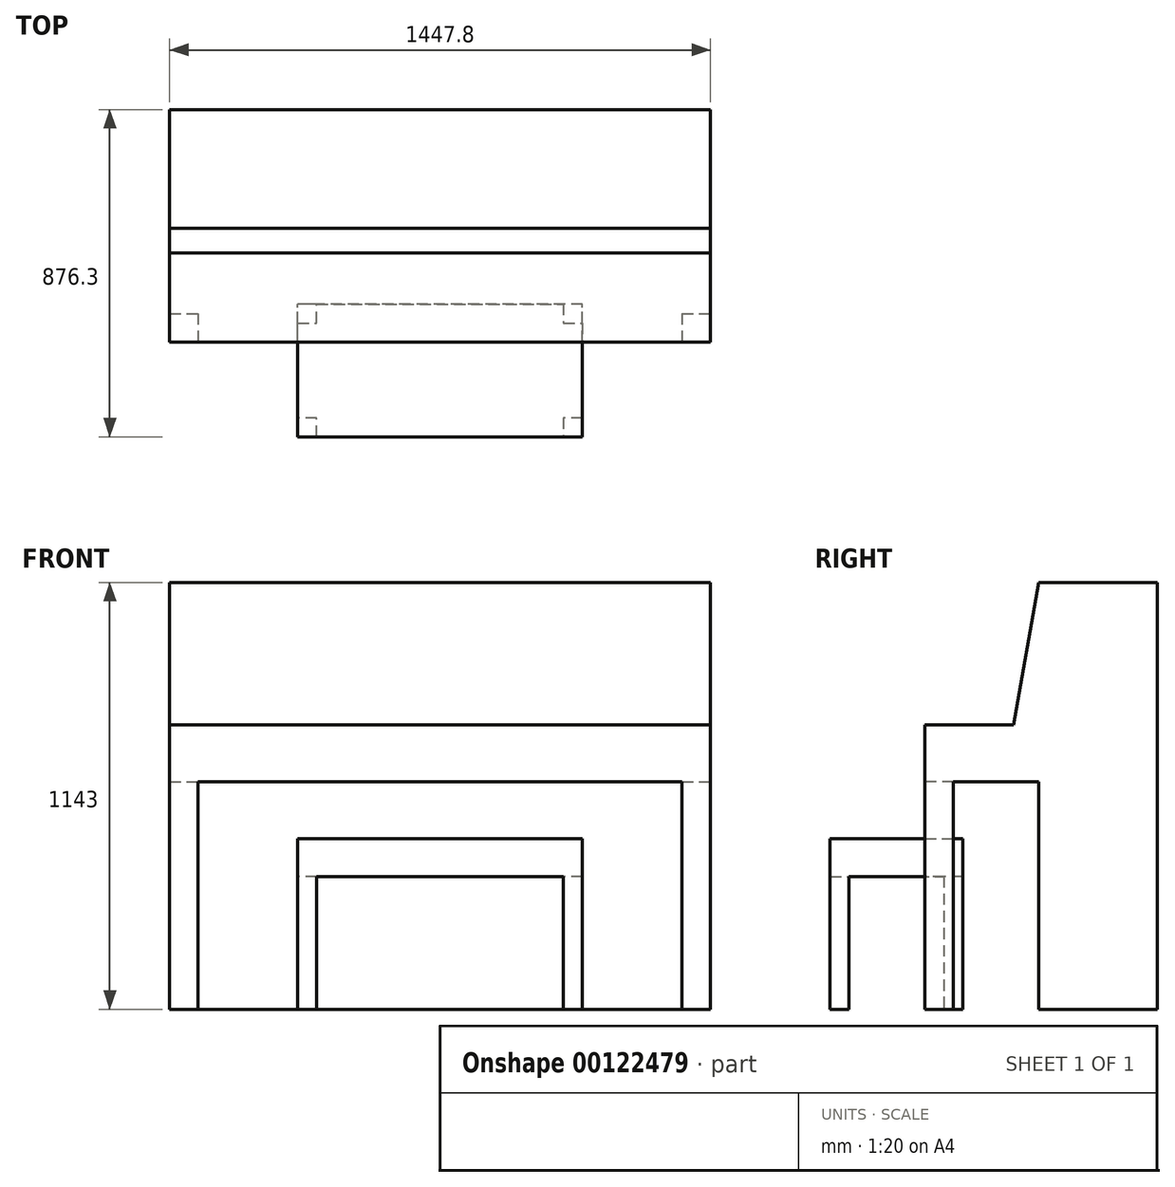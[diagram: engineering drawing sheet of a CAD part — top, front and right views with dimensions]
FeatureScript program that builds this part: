
annotation { "Feature Type Name" : "Feature", "Feature Type Description" : "" }
export const myFeature = defineFeature(function(context is Context, id is Id, definition is map)
    precondition{}
    {
        {
            var Q0;
            Q0=qCreatedBy(makeId("Top.planeOp"),FACE);
            var sketch = newSketch(context, id + "F0", { "sketchPlane" : qUnion([Q0])});
            skLineSegment(sketch, "E0.bottom", {"start": v(0, 0) * mm, "end": v(1447.8, 0) * mm});
            skLineSegment(sketch, "E0.top", {"start": v(0, -622.3) * mm, "end": v(1447.8, -622.3) * mm});
            skLineSegment(sketch, "E0.left", {"start": v(0, 0) * mm, "end": v(0, -622.3) * mm});
            skLineSegment(sketch, "E0.right", {"start": v(1447.8, 0) * mm, "end": v(1447.8, -622.3) * mm});
            skSolve(sketch);
        }
        {
            var Q0;
            Q0 = qSketchRegion(id + "F0", true);
            extrude(context, id + "F1", {"entities" : qUnion([Q0]), "depth" : 1143 * mm});
        }
        {
            var Q0;
            Q0=makeQuery(id+"F1.opExtrude","SWEPT_FACE",FACE,{"disambiguationData":[OSD([sQuery(id+"F0.wireOp",EDGE,"E0.right")])]});
            var sketch = newSketch(context, id + "F2", { "sketchPlane" : qUnion([Q0])});
            skLineSegment(sketch, "E1", {"start": v(-622.3, 1143) * mm, "end": v(-622.3, 762) * mm});
            skLineSegment(sketch, "E2", {"start": v(-622.3, 762) * mm, "end": v(-384.68, 762) * mm});
            skLineSegment(sketch, "E3", {"start": v(-384.68, 762) * mm, "end": v(-317.5, 1143) * mm});
            skLineSegment(sketch, "E4", {"start": v(-317.5, 1143) * mm, "end": v(-622.3, 1143) * mm});
            skSolve(sketch);
        }
        {
            var Q0;
            Q0 = qSketchRegion(id + "F2", true);
            extrude(context, id + "F3", {"entities" : qUnion([Q0]), "operationType" : NewBodyOperationType.REMOVE, "endBound" : BoundingType.THROUGH_ALL, "oppositeDirection" : true, "depth" : 25.4 * mm});
        }
        {
            var Q0;
            Q0=makeQuery(id+"F1.opExtrude","SWEPT_FACE",FACE,{"disambiguationData":[OSD([sQuery(id+"F0.wireOp",EDGE,"E0.top")])]});
            var sketch = newSketch(context, id + "F4", { "sketchPlane" : qUnion([Q0])});
            skLineSegment(sketch, "E5.bottom", {"start": v(76.2, 0) * mm, "end": v(1371.6, 0) * mm});
            skLineSegment(sketch, "E5.top", {"start": v(76.2, 609.6) * mm, "end": v(1371.6, 609.6) * mm});
            skLineSegment(sketch, "E5.left", {"start": v(76.2, 0) * mm, "end": v(76.2, 609.6) * mm});
            skLineSegment(sketch, "E5.right", {"start": v(1371.6, 0) * mm, "end": v(1371.6, 609.6) * mm});
            skPoint(sketch, "E5.middle", {"position": v(723.9, 304.8) * mm});
            skSolve(sketch);
        }
        {
            var Q0;
            Q0 = qSketchRegion(id + "F4", true);
            extrude(context, id + "F5", {"entities" : qUnion([Q0]), "operationType" : NewBodyOperationType.REMOVE, "oppositeDirection" : true, "depth" : 304.8 * mm});
        }
        {
            var Q0;
            Q0=makeQuery(id+"F1.opExtrude","SWEPT_FACE",FACE,{"disambiguationData":[OSD([sQuery(id+"F0.wireOp",EDGE,"E0.right")])]});
            var sketch = newSketch(context, id + "F6", { "sketchPlane" : qUnion([Q0])});
            skLineSegment(sketch, "E6.bottom", {"start": v(-546.1, 0) * mm, "end": v(-317.5, 0) * mm});
            skLineSegment(sketch, "E6.top", {"start": v(-546.1, 609.6) * mm, "end": v(-317.5, 609.6) * mm});
            skLineSegment(sketch, "E6.left", {"start": v(-546.1, 0) * mm, "end": v(-546.1, 609.6) * mm});
            skLineSegment(sketch, "E6.right", {"start": v(-317.5, 0) * mm, "end": v(-317.5, 609.6) * mm});
            skPoint(sketch, "E6.middle", {"position": v(-431.8, 304.8) * mm});
            skSolve(sketch);
        }
        {
            var Q0;
            Q0 = qSketchRegion(id + "F6", true);
            extrude(context, id + "F7", {"entities" : qUnion([Q0]), "operationType" : NewBodyOperationType.REMOVE, "endBound" : BoundingType.THROUGH_ALL, "oppositeDirection" : true, "depth" : 25.4 * mm});
        }
        {
            var Q0;
            Q0=qCreatedBy(makeId("Top.planeOp"),FACE);
            var sketch = newSketch(context, id + "F8", { "sketchPlane" : qUnion([Q0])});
            skLineSegment(sketch, "E7.bottom", {"start": v(1104.9, -876.3) * mm, "end": v(342.9, -876.3) * mm});
            skLineSegment(sketch, "E7.top", {"start": v(1104.9, -520.7) * mm, "end": v(342.9, -520.7) * mm});
            skLineSegment(sketch, "E7.left", {"start": v(1104.9, -876.3) * mm, "end": v(1104.9, -520.7) * mm});
            skLineSegment(sketch, "E7.right", {"start": v(342.9, -876.3) * mm, "end": v(342.9, -520.7) * mm});
            skPoint(sketch, "E7.middle", {"position": v(723.9, -698.5) * mm});
            skLineSegment(sketch, "E8", {"start": v(723.9, -698.5) * mm, "end": v(723.9, 0) * mm, "construction": true});
            skSolve(sketch);
        }
        {
            var Q0;
            Q0=qCreatedBy(makeId("Top.planeOp"),FACE);
            var sketch = newSketch(context, id + "F9", { "sketchPlane" : qUnion([Q0])});
            skLineSegment(sketch, "E9", {"start": v(342.9, -825.5) * mm, "end": v(342.9, -571.5) * mm});
            skLineSegment(sketch, "E10", {"start": v(342.9, -571.5) * mm, "end": v(393.7, -571.5) * mm});
            skLineSegment(sketch, "E11", {"start": v(393.7, -571.5) * mm, "end": v(393.7, -520.7) * mm});
            skLineSegment(sketch, "E12", {"start": v(393.7, -520.7) * mm, "end": v(1054.1, -520.7) * mm});
            skLineSegment(sketch, "E13", {"start": v(1054.1, -520.7) * mm, "end": v(1054.1, -571.5) * mm});
            skLineSegment(sketch, "E14", {"start": v(1054.1, -571.5) * mm, "end": v(1104.9, -571.5) * mm});
            skLineSegment(sketch, "E15", {"start": v(1104.9, -571.5) * mm, "end": v(1104.9, -825.5) * mm});
            skLineSegment(sketch, "E16", {"start": v(1104.9, -825.5) * mm, "end": v(1054.1, -825.5) * mm});
            skLineSegment(sketch, "E17", {"start": v(1054.1, -825.5) * mm, "end": v(1054.1, -876.3) * mm});
            skLineSegment(sketch, "E18", {"start": v(1054.1, -876.3) * mm, "end": v(393.7, -876.3) * mm});
            skLineSegment(sketch, "E19", {"start": v(393.7, -876.3) * mm, "end": v(393.7, -825.5) * mm});
            skLineSegment(sketch, "E20", {"start": v(393.7, -825.5) * mm, "end": v(342.9, -825.5) * mm});
            skSolve(sketch);
        }
        {
            var Q0;
            Q0 = qSketchRegion(id + "F8", true);
            extrude(context, id + "F10", {"entities" : qUnion([Q0]), "depth" : 457.2 * mm});
        }
        {
            var Q0;
            Q0 = qSketchRegion(id + "F9", true);
            var Q1;
            Q1=makeQuery(id+"F10.opExtrude","CAP_FACE",FACE,{"disambiguationData":[OSD([sQuery(id+"F8.wireOp",EDGE,"E7.bottom"),sQuery(id+"F8.wireOp",EDGE,"E7.top"),sQuery(id+"F8.wireOp",EDGE,"E7.left"),sQuery(id+"F8.wireOp",EDGE,"E7.right")])],"isStart":false});
            extrude(context, id + "F11", {"entities" : qUnion([Q0]), "operationType" : NewBodyOperationType.REMOVE, "endBoundEntityFace" : qUnion([Q1]), "depth" : 355.6 * mm});
        }
    });
